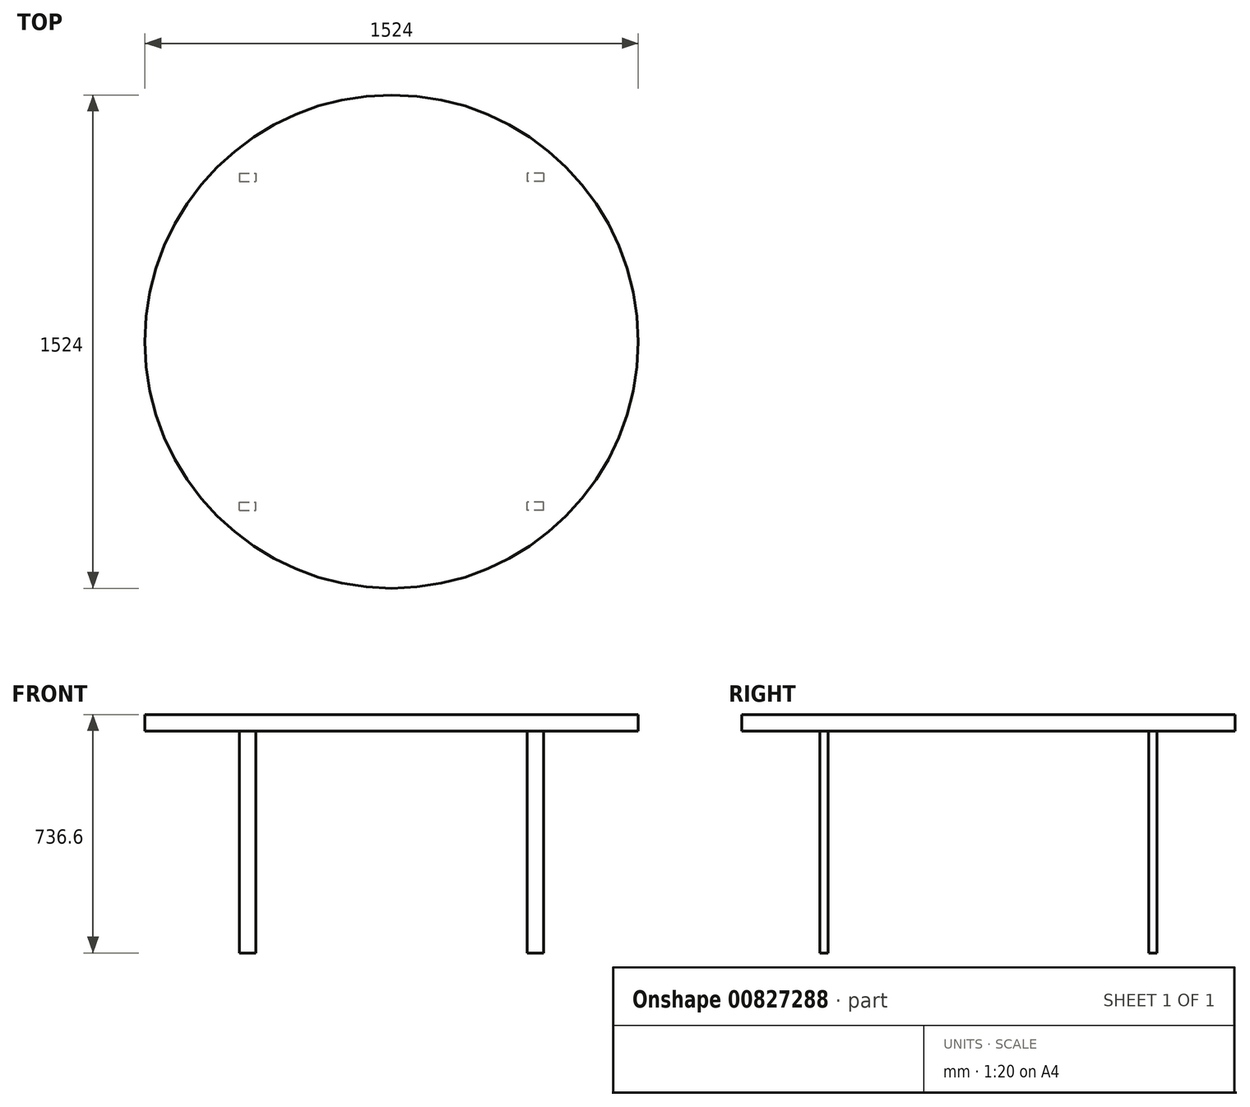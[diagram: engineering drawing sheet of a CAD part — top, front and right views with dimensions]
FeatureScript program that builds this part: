
annotation { "Feature Type Name" : "Feature", "Feature Type Description" : "" }
export const myFeature = defineFeature(function(context is Context, id is Id, definition is map)
    precondition{}
    {
        {
            var Q0;
            Q0=qCreatedBy(makeId("Top.planeOp"),FACE);
            var sketch = newSketch(context, id + "F0", { "sketchPlane" : qUnion([Q0])});
            skCircle(sketch, "E0", {"center": v(0, 0) * mm, "radius": 762 * mm});
            skSolve(sketch);
        }
        {
            var Q0;
            Q0=qSketchRegion(id+"F0",true);
            extrude(context, id + "F1", {"entities" : qUnion([Q0]), "depth" : 50.8 * mm});
        }
        {
            var Q0;
            Q0=makeQuery(id+"F1.opExtrude","CAP_FACE",FACE,{"disambiguationData":[OSD([sQuery(id+"F0.wireOp",EDGE,"E0")])],"isStart":true});
            var sketch = newSketch(context, id + "F2", { "sketchPlane" : qUnion([Q0])});
            skLineSegment(sketch, "E1.bottom", {"start": v(-469.9, 520.7) * mm, "end": v(-419.1, 520.7) * mm});
            skLineSegment(sketch, "E1.top", {"start": v(-469.9, 495.3) * mm, "end": v(-419.1, 495.3) * mm});
            skLineSegment(sketch, "E1.left", {"start": v(-469.9, 520.7) * mm, "end": v(-469.9, 495.3) * mm});
            skLineSegment(sketch, "E1.right", {"start": v(-419.1, 520.7) * mm, "end": v(-419.1, 495.3) * mm});
            skLineSegment(sketch, "E2", {"start": v(-776.18, 0) * mm, "end": v(757.65, 0) * mm, "construction": true});
            skLineSegment(sketch, "E3", {"start": v(0, 738.51) * mm, "end": v(0, -712.07) * mm, "construction": true});
            skLineSegment(sketch, "E4.MirrorCS", {"start": v(469.9, 520.7) * mm, "end": v(419.1, 520.7) * mm});
            skLineSegment(sketch, "E5.MirrorCS", {"start": v(469.9, 520.7) * mm, "end": v(469.9, 495.3) * mm});
            skLineSegment(sketch, "E6.MirrorCS", {"start": v(419.1, 520.7) * mm, "end": v(419.1, 495.3) * mm});
            skLineSegment(sketch, "E7.MirrorCS", {"start": v(469.9, 495.3) * mm, "end": v(419.1, 495.3) * mm});
            skLineSegment(sketch, "E8.MirrorCS", {"start": v(-469.9, -495.3) * mm, "end": v(-419.1, -495.3) * mm});
            skLineSegment(sketch, "E9.MirrorCS", {"start": v(-469.9, -520.7) * mm, "end": v(-469.9, -495.3) * mm});
            skLineSegment(sketch, "E10.MirrorCS", {"start": v(-469.9, -520.7) * mm, "end": v(-419.1, -520.7) * mm});
            skLineSegment(sketch, "E11.MirrorCS", {"start": v(-419.1, -520.7) * mm, "end": v(-419.1, -495.3) * mm});
            skLineSegment(sketch, "E12.MirrorCS", {"start": v(469.9, -520.7) * mm, "end": v(419.1, -520.7) * mm});
            skLineSegment(sketch, "E13.MirrorCS", {"start": v(469.9, -495.3) * mm, "end": v(419.1, -495.3) * mm});
            skLineSegment(sketch, "E14.MirrorCS", {"start": v(469.9, -520.7) * mm, "end": v(469.9, -495.3) * mm});
            skLineSegment(sketch, "E15.MirrorCS", {"start": v(419.1, -520.7) * mm, "end": v(419.1, -495.3) * mm});
            skSolve(sketch);
        }
        {
            var Q0;
            Q0=qSketchRegion(id+"F2",true);
            extrude(context, id + "F3", {"entities" : qUnion([Q0]), "operationType" : NewBodyOperationType.ADD, "depth" : 685.8 * mm});
        }
    });
